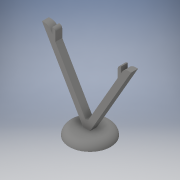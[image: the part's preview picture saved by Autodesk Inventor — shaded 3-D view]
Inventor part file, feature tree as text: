
AUTODESK INVENTOR PART (.ipt)
format: ipt  version: 2019.2 (Build 232265000, 265)  size: 169,472 bytes
history: native  units: in
note: dims shown in document units (in); Inventor stores cm internally (conversion verified against a paired STEP export)
features: fillet x4, extrude x3, sketch x3
ambient origin geometry x8: Origin, YZ Plane, XZ Plane, XY Plane, X Axis, Y Axis, Z Axis, Center Point
bodies: Solid1 (feature_tree)
feature tree (10):
  extrude  "Extrusion1"  Depth=0.5in TaperAngle=0.0deg
  extrude  "Extrusion2"  Depth=0.5in TaperAngle=0.0deg
  fillet  "Fillet1"  Radius=0.5in
  fillet  "Fillet2"  Radius=0.1125in
  extrude  "Extrusion4"  Depth=0.225in
  fillet  "Fillet5"  Radius=0.5in
  fillet  "Fillet6"  Radius=0.2125in
  sketch  "Sketch1"  dims[d2=0.25in d5=0.5in d6=0.0in]
  sketch  "Sketch2"  dims[d7=3.0in d8=0.5in d9=0.0in d10=0.5in d11=0.1125in]
  sketch  "Sketch4"  dims[d19=0.5in d20=0.225in d21=0.5in d22=0.0in d23=0.2125in d24=0.525in]
